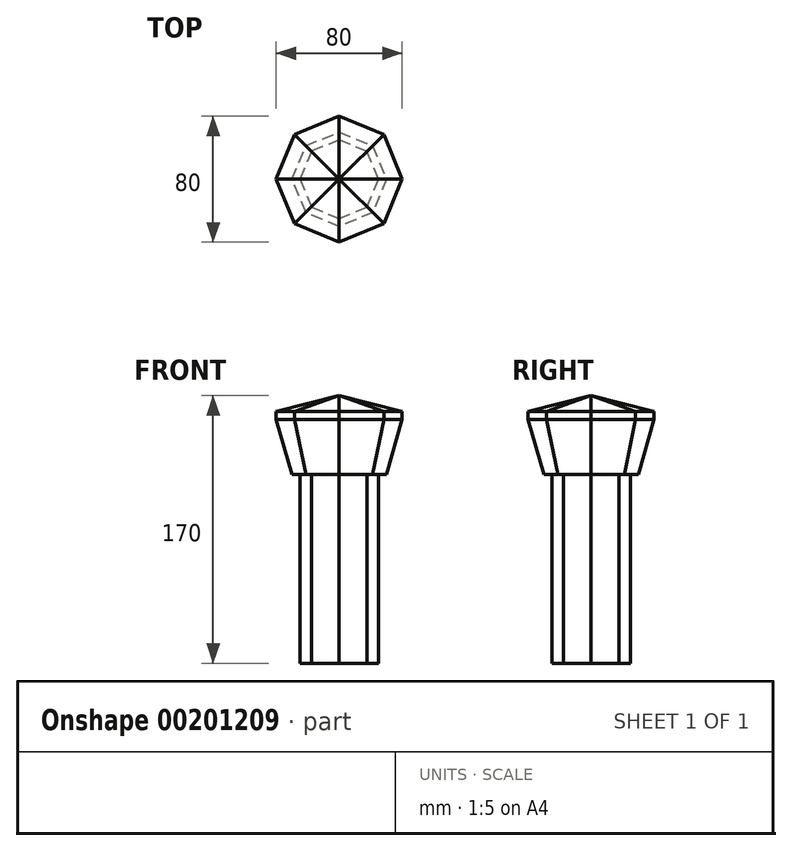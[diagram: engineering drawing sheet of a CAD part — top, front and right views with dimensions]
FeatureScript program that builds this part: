
annotation { "Feature Type Name" : "Feature", "Feature Type Description" : "" }
export const myFeature = defineFeature(function(context is Context, id is Id, definition is map)
    precondition{}
    {
        {
            var Q0;
            Q0=qCreatedBy(makeId("Front.planeOp"),FACE);
            var sketch = newSketch(context, id + "F0", { "sketchPlane" : qUnion([Q0])});
            skLineSegment(sketch, "E0", {"start": v(0, 0) * mm, "end": v(25, 0) * mm});
            skLineSegment(sketch, "E1", {"start": v(25, 0) * mm, "end": v(25, 120) * mm});
            skLineSegment(sketch, "E2", {"start": v(25, 120) * mm, "end": v(30, 120) * mm});
            skLineSegment(sketch, "E3", {"start": v(30, 120) * mm, "end": v(40, 155) * mm});
            skLineSegment(sketch, "E4", {"start": v(40, 155) * mm, "end": v(40, 160) * mm});
            skLineSegment(sketch, "E5", {"start": v(40, 160) * mm, "end": v(0, 170) * mm});
            skLineSegment(sketch, "E6", {"start": v(0, 170) * mm, "end": v(0, 0) * mm});
            skSolve(sketch);
        }
        {
            var Q0;
            Q0=qCreatedBy(makeId("Front.planeOp"),FACE);
            var Q1;
            Q1=sQuery(id+"F0.wireOp",EDGE,"E6");
            cPlane(context, id + "F1", {"entities" : qUnion([Q0, Q1]), "cplaneType" : CPlaneType.LINE_ANGLE, "offset" : 25 * mm, "angle" : 135 * degree, "width" : 150 * mm, "height" : 150 * mm});
        }
        {
            var Q0;
            Q0=qCreatedBy(id+"F1.planeOp",FACE);
            var sketch = newSketch(context, id + "F2", { "sketchPlane" : qUnion([Q0])});
            skLineSegment(sketch, "E7", {"start": v(0, 0) * mm, "end": v(25, 0) * mm});
            skLineSegment(sketch, "E8", {"start": v(25, 0) * mm, "end": v(25, 120) * mm});
            skLineSegment(sketch, "E9", {"start": v(25, 120) * mm, "end": v(30, 120) * mm});
            skLineSegment(sketch, "E10", {"start": v(30, 120) * mm, "end": v(40, 155) * mm});
            skLineSegment(sketch, "E11", {"start": v(40, 155) * mm, "end": v(40, 160) * mm});
            skLineSegment(sketch, "E12", {"start": v(40, 160) * mm, "end": v(0, 170) * mm});
            skLineSegment(sketch, "E13", {"start": v(0, 170) * mm, "end": v(0, 0) * mm});
            skSolve(sketch);
        }
        {
            var Q0;
            Q0=qCreatedBy(makeId("Top.planeOp"),FACE);
            var sketch = newSketch(context, id + "F3", { "sketchPlane" : qUnion([Q0])});
            skLineSegment(sketch, "E14", {"start": v(25, 0) * mm, "end": v(17.68, 17.68) * mm});
            skSolve(sketch);
        }
        {
            var Q0;
            Q0=makeQuery(id+"F2.imprint","IMPRINT",FACE,{"disambiguationData":[TD([[makeQuery(id+"F2.imprint","IMPRINT",EDGE,{"derivedFrom":sQuery(id+"F2.wireOp",EDGE,"E7")}),1.0]])]});
            var Q1;
            Q1=makeQuery(id+"F0.imprint","IMPRINT",FACE,{"disambiguationData":[TD([[makeQuery(id+"F0.imprint","IMPRINT",EDGE,{"derivedFrom":sQuery(id+"F0.wireOp",EDGE,"E0")}),1.0]])]});
            var Q2;
            Q2=sQuery(id+"F3.wireOp",EDGE,"E14");
            loft(context, id + "F4", {"addGuides" : true, "sheetProfilesArray" : [{ "sheetProfileEntities" : qUnion([Q0]) }, { "sheetProfileEntities" : qUnion([Q1]) }], "guidesArray" : [{ "guideEntities" : qUnion([Q2]), "guideDerivativeType" : LoftGuideDerivativeType.DEFAULT, "guideDerivativeMagnitude" : 1 }]});
        }
        {
            var Q0;
            Q0=makeQuery(id+"F4.opLoft","SWEPT_BODY",BODY,{"disambiguationData":[OSD([makeQuery(id+"F0.imprint","IMPRINT",FACE,{"disambiguationData":[TD([[makeQuery(id+"F0.imprint","IMPRINT",EDGE,{"derivedFrom":sQuery(id+"F0.wireOp",EDGE,"E0")}),1.0]])]}),makeQuery(id+"F2.imprint","IMPRINT",FACE,{"disambiguationData":[TD([[makeQuery(id+"F2.imprint","IMPRINT",EDGE,{"derivedFrom":sQuery(id+"F2.wireOp",EDGE,"E7")}),1.0]])]}),sQuery(id+"F3.wireOp",EDGE,"E14")])]});
            var Q1;
            Q1=makeQuery(id+"F4.opLoft","CAP_EDGE",EDGE,{"disambiguationData":[OSD([sQuery(id+"F0.wireOp",EDGE,"E6"),sQuery(id+"F2.wireOp",EDGE,"E13")])],"isStart":false});
            circularPattern(context, id + "F5", {"entities" : qUnion([Q0]), "axis" : qUnion([Q1]), "angle" : 360 * degree, "instanceCount" : 8, "equalSpace" : true});
        }
    });
